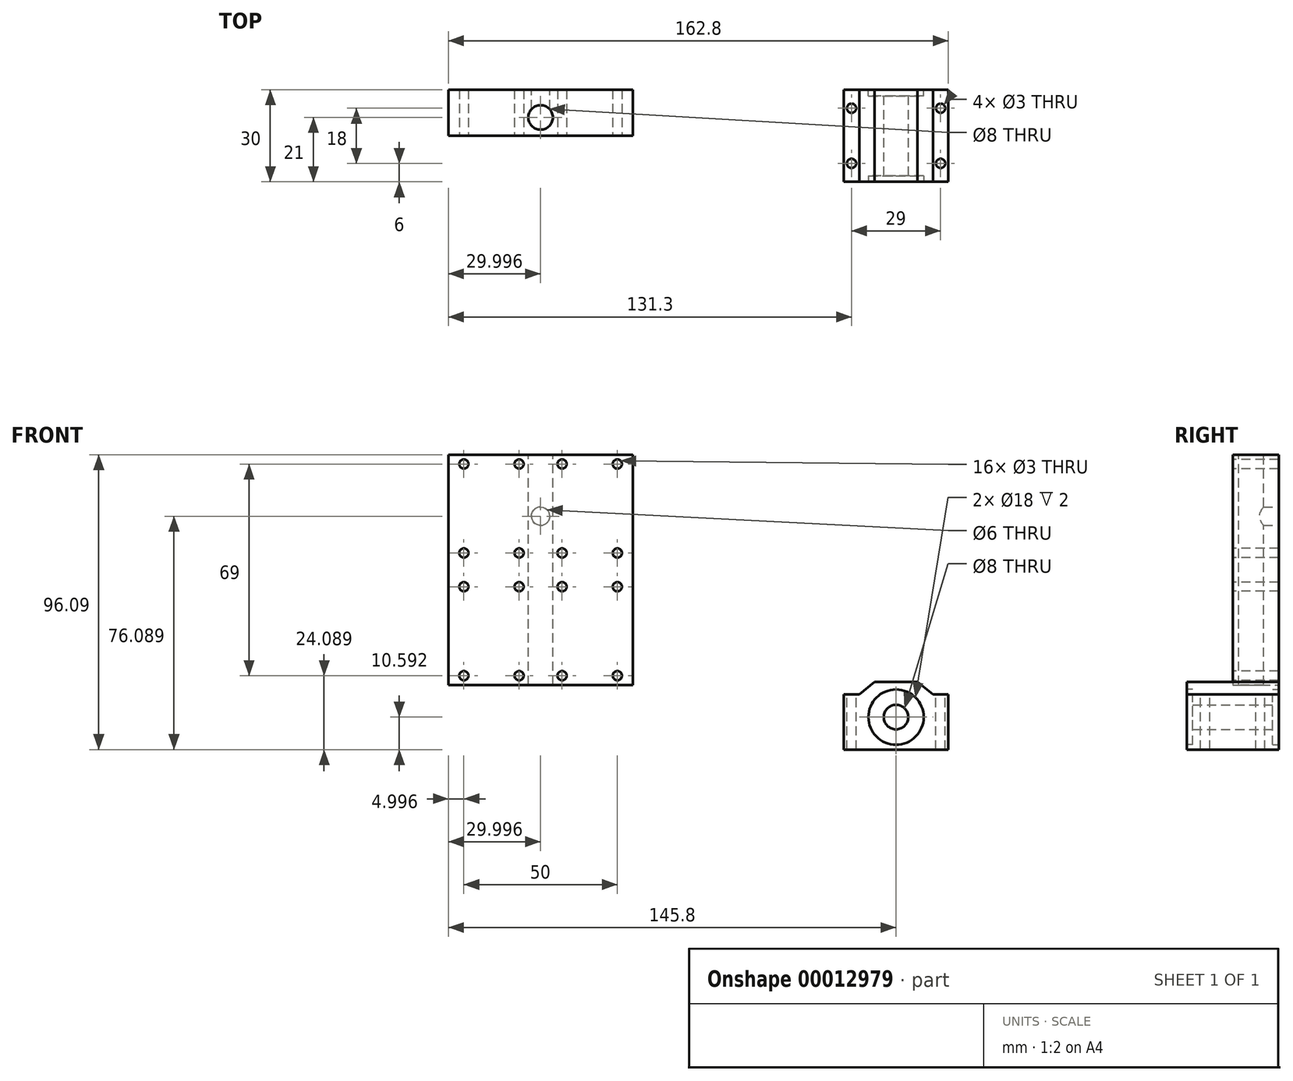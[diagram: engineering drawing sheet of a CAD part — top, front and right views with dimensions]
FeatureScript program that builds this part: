
annotation { "Feature Type Name" : "Feature", "Feature Type Description" : "" }
export const myFeature = defineFeature(function(context is Context, id is Id, definition is map)
    precondition{}
    {
        {
            var Q0;
            Q0=qCreatedBy(makeId("Front.planeOp"),FACE);
            var sketch = newSketch(context, id + "F0", { "sketchPlane" : qUnion([Q0])});
            skLineSegment(sketch, "E0", {"start": v(0, 0) * mm, "end": v(17, 0) * mm});
            skLineSegment(sketch, "E1", {"start": v(17, 0) * mm, "end": v(17, 18) * mm});
            skLineSegment(sketch, "E2", {"start": v(17, 18) * mm, "end": v(12, 18) * mm});
            skLineSegment(sketch, "E3", {"start": v(12, 18) * mm, "end": v(7, 22) * mm});
            skLineSegment(sketch, "E4", {"start": v(7, 22) * mm, "end": v(0, 22) * mm});
            skLineSegment(sketch, "E5.MirrorCS", {"start": v(-7, 22) * mm, "end": v(0, 22) * mm});
            skLineSegment(sketch, "E6.MirrorCS", {"start": v(-12, 18) * mm, "end": v(-7, 22) * mm});
            skLineSegment(sketch, "E7.MirrorCS", {"start": v(-17, 18) * mm, "end": v(-12, 18) * mm});
            skLineSegment(sketch, "E8.MirrorCS", {"start": v(-17, 0) * mm, "end": v(-17, 18) * mm});
            skLineSegment(sketch, "E9.MirrorCS", {"start": v(0, 0) * mm, "end": v(-17, 0) * mm});
            skCircle(sketch, "E10", {"center": v(0, 10.6) * mm, "radius": 4 * mm});
            skCircle(sketch, "E11.0", {"center": v(0, 10.6) * mm, "radius": 9 * mm});
            skSolve(sketch);
        }
        {
            var Q0;
            Q0 = qSketchRegion(id + "F0", true);
            var Q1;
            Q1=makeQuery(id+"F0.imprint","IMPRINT",FACE,{"disambiguationData":[TD([[makeQuery(id+"F0.imprint","IMPRINT",EDGE,{"derivedFrom":sQuery(id+"F0.wireOp",EDGE,"E10")}),-1.0]])]});
            extrude(context, id + "F1", {"entities" : qUnion([Q0, Q1]), "depth" : 30 * mm});
        }
        {
            var Q0;
            Q0=makeQuery(id+"F1.opExtrude","SWEPT_FACE",FACE,{"disambiguationData":[OSD([sQuery(id+"F0.wireOp",EDGE,"E7.MirrorCS")])]});
            var sketch = newSketch(context, id + "F2", { "sketchPlane" : qUnion([Q0])});
            skCircle(sketch, "E12", {"center": v(-14.5, -6) * mm, "radius": 1.5 * mm});
            skPoint(sketch, "E12.centerSnap0", {"position": v(-14.5, 0) * mm});
            skCircle(sketch, "E13", {"center": v(-14.5, -24) * mm, "radius": 1.5 * mm});
            skPoint(sketch, "E13.centerSnap0", {"position": v(-14.5, -30) * mm});
            skCircle(sketch, "E14.MirrorC", {"center": v(14.5, -24) * mm, "radius": 1.5 * mm});
            skCircle(sketch, "E15.MirrorC", {"center": v(14.5, -6) * mm, "radius": 1.5 * mm});
            skSolve(sketch);
        }
        {
            var Q0;
            Q0 = qSketchRegion(id + "F2", true);
            extrude(context, id + "F3", {"entities" : qUnion([Q0]), "operationType" : NewBodyOperationType.REMOVE, "endBound" : BoundingType.THROUGH_ALL, "oppositeDirection" : true, "depth" : 25 * mm});
        }
        {
            var Q0;
            Q0=makeQuery(id+"F0.imprint","IMPRINT",FACE,{"disambiguationData":[TD([[makeQuery(id+"F0.imprint","IMPRINT",EDGE,{"derivedFrom":sQuery(id+"F0.wireOp",EDGE,"E10")}),-1.0]])]});
            extrude(context, id + "F4", {"entities" : qUnion([Q0]), "operationType" : NewBodyOperationType.REMOVE, "depth" : 2 * mm});
        }
        {
            var Q0;
            Q0=makeQuery(id+"F1.opExtrude","CAP_FACE",FACE,{"disambiguationData":[OSD([sQuery(id+"F0.wireOp",EDGE,"E0"),sQuery(id+"F0.wireOp",EDGE,"E1"),sQuery(id+"F0.wireOp",EDGE,"E2"),sQuery(id+"F0.wireOp",EDGE,"E3"),sQuery(id+"F0.wireOp",EDGE,"E4"),sQuery(id+"F0.wireOp",EDGE,"E5.MirrorCS"),sQuery(id+"F0.wireOp",EDGE,"E6.MirrorCS"),sQuery(id+"F0.wireOp",EDGE,"E7.MirrorCS"),sQuery(id+"F0.wireOp",EDGE,"E8.MirrorCS"),sQuery(id+"F0.wireOp",EDGE,"E9.MirrorCS"),sQuery(id+"F0.wireOp",EDGE,"E10")])],"isStart":false});
            var sketch = newSketch(context, id + "F5", { "sketchPlane" : qUnion([Q0])});
            skCircle(sketch, "E16.0", {"center": v(0, 10.6) * mm, "radius": 9 * mm});
            skSolve(sketch);
        }
        {
            var Q0;
            Q0=makeQuery(id+"F5.imprint","IMPRINT",FACE,{"disambiguationData":[TD([[makeQuery(id+"F5.imprint","IMPRINT",EDGE,{"derivedFrom":sQuery(id+"F5.wireOp",EDGE,"E16.0")}),1.0]])]});
            extrude(context, id + "F6", {"entities" : qUnion([Q0]), "operationType" : NewBodyOperationType.REMOVE, "oppositeDirection" : true, "depth" : 2 * mm});
        }
        {
            var Q0;
            Q0=qCreatedBy(makeId("Front.planeOp"),FACE);
            var sketch = newSketch(context, id + "F7", { "sketchPlane" : qUnion([Q0])});
            skLineSegment(sketch, "E17.bottom", {"start": v(-145.8, 96.09) * mm, "end": v(-85.8, 96.09) * mm});
            skLineSegment(sketch, "E17.top", {"start": v(-145.8, 21.09) * mm, "end": v(-85.8, 21.09) * mm});
            skLineSegment(sketch, "E17.left", {"start": v(-145.8, 96.09) * mm, "end": v(-145.8, 21.09) * mm});
            skLineSegment(sketch, "E17.right", {"start": v(-85.8, 96.09) * mm, "end": v(-85.8, 21.09) * mm});
            skSolve(sketch);
        }
        {
            var Q0;
            Q0 = qSketchRegion(id + "F7", true);
            extrude(context, id + "F8", {"entities" : qUnion([Q0]), "depth" : 15 * mm});
        }
        {
            var Q0;
            Q0=makeQuery(id+"F8.opExtrude","CAP_FACE",FACE,{"disambiguationData":[OSD([sQuery(id+"F7.wireOp",EDGE,"E17.bottom"),sQuery(id+"F7.wireOp",EDGE,"E17.top"),sQuery(id+"F7.wireOp",EDGE,"E17.left"),sQuery(id+"F7.wireOp",EDGE,"E17.right")])],"isStart":false});
            var sketch = newSketch(context, id + "F9", { "sketchPlane" : qUnion([Q0])});
            skLineSegment(sketch, "E18", {"start": v(-145.8, 78.59) * mm, "end": v(-85.8, 78.59) * mm, "construction": true});
            skLineSegment(sketch, "E19", {"start": v(-145.8, 58.59) * mm, "end": v(-85.8, 58.59) * mm, "construction": true});
            skLineSegment(sketch, "E20", {"start": v(-145.8, 93.09) * mm, "end": v(-85.8, 93.09) * mm, "construction": true});
            skLineSegment(sketch, "E21", {"start": v(-145.8, 71.54) * mm, "end": v(-85.8, 71.54) * mm, "construction": true});
            skCircle(sketch, "E22", {"center": v(-140.8, 93.09) * mm, "radius": 1.5 * mm});
            skCircle(sketch, "E23", {"center": v(-122.8, 93.09) * mm, "radius": 1.5 * mm});
            skCircle(sketch, "E24", {"center": v(-108.8, 93.09) * mm, "radius": 1.5 * mm});
            skCircle(sketch, "E25", {"center": v(-90.8, 93.09) * mm, "radius": 1.5 * mm});
            skCircle(sketch, "E26.MirrorC", {"center": v(-140.8, 64.09) * mm, "radius": 1.5 * mm});
            skCircle(sketch, "E27.MirrorC", {"center": v(-122.8, 64.09) * mm, "radius": 1.5 * mm});
            skCircle(sketch, "E28.MirrorC", {"center": v(-108.8, 64.09) * mm, "radius": 1.5 * mm});
            skCircle(sketch, "E29.MirrorC", {"center": v(-90.8, 64.09) * mm, "radius": 1.5 * mm});
            skCircle(sketch, "E30.MirrorC", {"center": v(-140.8, 24.09) * mm, "radius": 1.5 * mm});
            skCircle(sketch, "E31.MirrorC", {"center": v(-122.8, 53.09) * mm, "radius": 1.5 * mm});
            skCircle(sketch, "E32.MirrorC", {"center": v(-108.8, 53.09) * mm, "radius": 1.5 * mm});
            skCircle(sketch, "E33.MirrorC", {"center": v(-90.8, 53.09) * mm, "radius": 1.5 * mm});
            skCircle(sketch, "E34.MirrorC", {"center": v(-140.8, 53.09) * mm, "radius": 1.5 * mm});
            skCircle(sketch, "E35.MirrorC", {"center": v(-122.8, 24.09) * mm, "radius": 1.5 * mm});
            skCircle(sketch, "E36.MirrorC", {"center": v(-108.8, 24.09) * mm, "radius": 1.5 * mm});
            skCircle(sketch, "E37.MirrorC", {"center": v(-90.8, 24.09) * mm, "radius": 1.5 * mm});
            skSolve(sketch);
        }
        {
            var Q0;
            Q0 = qSketchRegion(id + "F9", true);
            extrude(context, id + "F10", {"entities" : qUnion([Q0]), "operationType" : NewBodyOperationType.REMOVE, "oppositeDirection" : true, "depth" : 25 * mm});
        }
        {
            var Q0;
            Q0=makeQuery(id+"F8.opExtrude","CAP_FACE",FACE,{"disambiguationData":[OSD([sQuery(id+"F7.wireOp",EDGE,"E17.bottom"),sQuery(id+"F7.wireOp",EDGE,"E17.top"),sQuery(id+"F7.wireOp",EDGE,"E17.left"),sQuery(id+"F7.wireOp",EDGE,"E17.right")])],"isStart":true});
            var sketch = newSketch(context, id + "F11", { "sketchPlane" : qUnion([Q0])});
            skLineSegment(sketch, "E38", {"start": v(115.8, 96.09) * mm, "end": v(115.8, 21.09) * mm, "construction": true});
            skCircle(sketch, "E39", {"center": v(130.3, 89.09) * mm, "radius": 1.5 * mm});
            skCircle(sketch, "E40", {"center": v(130.3, 71.09) * mm, "radius": 1.5 * mm});
            skCircle(sketch, "E41", {"center": v(130.3, 46.09) * mm, "radius": 1.5 * mm});
            skCircle(sketch, "E42", {"center": v(130.3, 28.09) * mm, "radius": 1.5 * mm});
            skCircle(sketch, "E43.MirrorC", {"center": v(101.3, 71.09) * mm, "radius": 1.5 * mm});
            skCircle(sketch, "E44.MirrorC", {"center": v(101.3, 46.09) * mm, "radius": 1.5 * mm});
            skCircle(sketch, "E45.MirrorC", {"center": v(101.3, 28.09) * mm, "radius": 1.5 * mm});
            skCircle(sketch, "E46.MirrorC", {"center": v(101.3, 89.09) * mm, "radius": 1.5 * mm});
            skSolve(sketch);
        }
        {
            var Q0;
            Q0=makeQuery(id+"F8.opExtrude","SWEPT_FACE",FACE,{"disambiguationData":[OSD([sQuery(id+"F7.wireOp",EDGE,"E17.bottom")])]});
            var sketch = newSketch(context, id + "F12", { "sketchPlane" : qUnion([Q0])});
            skCircle(sketch, "E47", {"center": v(-115.8, -9) * mm, "radius": 4 * mm});
            skPoint(sketch, "E47.centerSnap0", {"position": v(-115.8, 0) * mm});
            skSolve(sketch);
        }
        {
            var Q0;
            Q0 = qSketchRegion(id + "F12", true);
            extrude(context, id + "F13", {"entities" : qUnion([Q0]), "operationType" : NewBodyOperationType.REMOVE, "endBound" : BoundingType.THROUGH_ALL, "oppositeDirection" : true, "depth" : 25 * mm});
        }
        {
            var Q0;
            Q0=makeQuery(id+"F11.imprint","IMPRINT",FACE,{"disambiguationData":[TD([[makeQuery(id+"F11.imprint","IMPRINT",EDGE,{"derivedFrom":sQuery(id+"F11.wireOp",EDGE,"E39")}),-1.0]])]});
            var sketch = newSketch(context, id + "F14", { "sketchPlane" : qUnion([Q0])});
            skCircle(sketch, "E48", {"center": v(115.8, 76.09) * mm, "radius": 3 * mm});
            skSolve(sketch);
        }
        {
            var Q0;
            Q0 = qSketchRegion(id + "F14", true);
            extrude(context, id + "F15", {"entities" : qUnion([Q0]), "operationType" : NewBodyOperationType.REMOVE, "oppositeDirection" : true, "depth" : 7 * mm});
        }
    });
